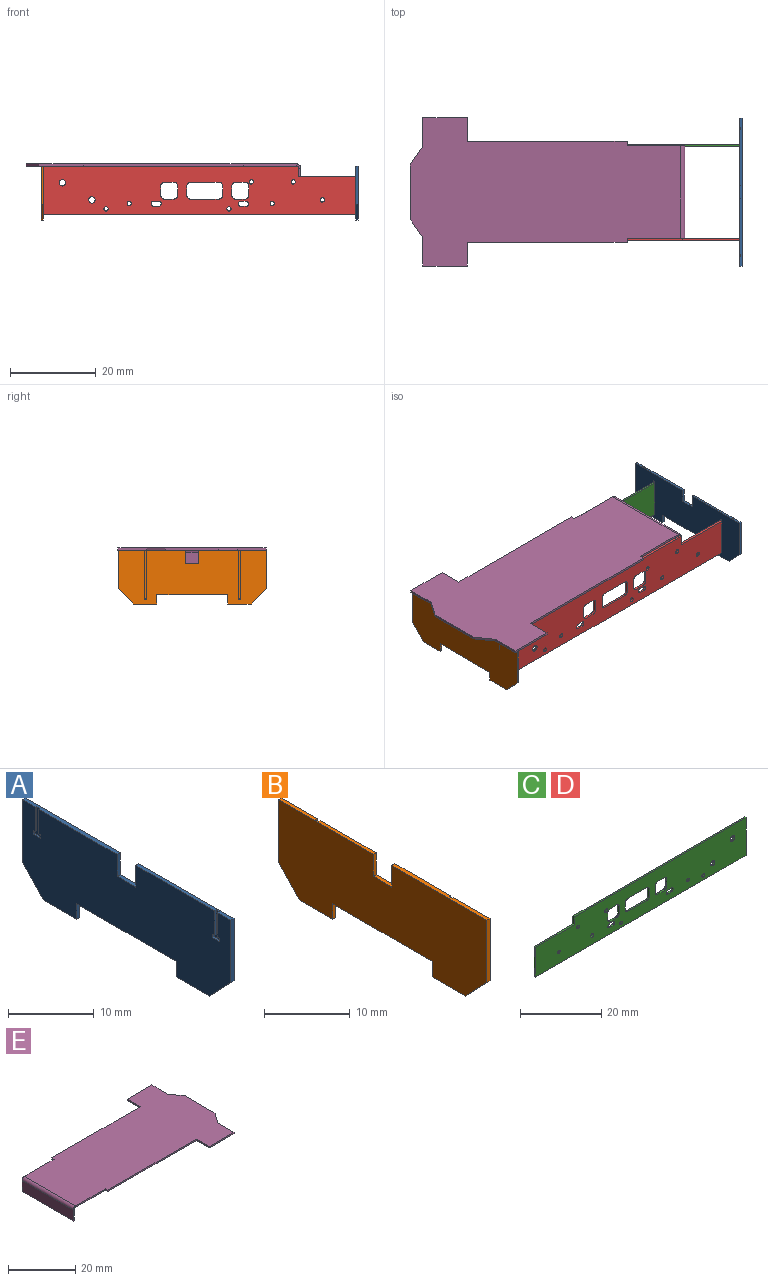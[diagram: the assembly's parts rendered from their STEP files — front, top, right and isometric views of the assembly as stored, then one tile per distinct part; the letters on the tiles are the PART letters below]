
ASSEMBLY  parts=5 mates=12
PART A: 42 faces, bbox 0.5x34.5x12.6 mm
  f0: plane 34.5x12.6mm, normal (-1,0,0), area 371.1mm2, adj f2,f3,f4,f5,f6,f7,f8,f9
  f1: plane 34.5x12.6mm, normal (1,0,0), area 366.4mm2, adj f2,f3,f4,f5,f6,f7,f8,f9
  f2: plane 3.1x0.5mm, normal (0,0,1), area 1.6mm2, adj f0,f1,f3,f23
  f3: plane 3.1x0.5mm, normal (0,1,0), area 1.5mm2, adj f0,f1,f2,f4
  f4: plane 15.7x0.5mm, normal (0,0,1), area 7.7mm2, adj f0,f1,f3,f5,f15,f21,f22
  f5: plane 8.9x0.5mm, normal (0,-1,0), area 4.4mm2, adj f0,f1,f4,f6
  f6: plane 3.7x3.5mm, normal (0,-0.73,-0.69), area 2.5mm2, adj f0,f1,f5,f7
  f7: plane 5.5x0.5mm, normal (0,0,-1), area 2.8mm2, adj f0,f1,f6,f8
  f8: plane 2.2x0.5mm, normal (0,1,0), area 1.1mm2, adj f0,f1,f7,f9
  f9: plane 16.5x0.5mm, normal (0,0,-1), area 8.2mm2, adj f0,f1,f8,f28
  f10: plane 0.5x0.25mm, normal (0,0,-1), area 0.1mm2, adj f1,f11,f13,f14
  f11: plane 9.4x0.25mm, normal (0,1,0), area 2.4mm2, adj f1,f10,f12,f14
  f12: plane 0.5x0.25mm, normal (0,0,1), area 0.1mm2, adj f1,f11,f13,f14
  f13: plane 9.4x0.25mm, normal (0,-1,0), area 2.4mm2, adj f1,f10,f12,f14
  f14: plane 9.4x0.5mm, normal (1,0,0), area 4.7mm2, adj f10,f11,f12,f13
  f15: plane 3.5x0.25mm, normal (0,-1,0), area 0.9mm2, adj f0,f4,f16,f22
  f16: plane 0.35x0.25mm, normal (0,0,-1), area 0.1mm2, adj f0,f15,f17,f22
  f17: plane 0.5x0.25mm, normal (0,-1,0), area 0.1mm2, adj f0,f16,f18,f22
  f18: plane 1.2x0.25mm, normal (0,0,1), area 0.3mm2, adj f0,f17,f19,f22
  f19: plane 0.5x0.25mm, normal (0,1,0), area 0.1mm2, adj f0,f18,f20,f22
  f20: plane 0.35x0.25mm, normal (0,0,-1), area 0.1mm2, adj f0,f19,f21,f22
  f21: plane 3.5x0.25mm, normal (0,1,0), area 0.9mm2, adj f0,f4,f20,f22
  f22: plane 4x1.2mm, normal (-1,0,0), area 2.3mm2, adj f4,f15,f16,f17,f18,f19,f20,f21
  f23: plane 3.1x0.5mm, normal (0,-1,0), area 1.5mm2, adj f0,f1,f2,f24
  f24: plane 15.7x0.5mm, normal (0,0,1), area 7.7mm2, adj f0,f1,f23,f25,f34,f40,f41
  f25: plane 8.9x0.5mm, normal (0,1,0), area 4.4mm2, adj f0,f1,f24,f26
  f26: plane 3.7x3.5mm, normal (0,0.73,-0.69), area 2.5mm2, adj f0,f1,f25,f27
  f27: plane 5.5x0.5mm, normal (0,0,-1), area 2.8mm2, adj f0,f1,f26,f28
  f28: plane 2.2x0.5mm, normal (0,-1,0), area 1.1mm2, adj f0,f1,f9,f27
  f29: plane 0.5x0.25mm, normal (0,0,-1), area 0.1mm2, adj f1,f30,f32,f33
  f30: plane 9.4x0.25mm, normal (0,-1,0), area 2.4mm2, adj f1,f29,f31,f33
  f31: plane 0.5x0.25mm, normal (0,0,1), area 0.1mm2, adj f1,f30,f32,f33
  f32: plane 9.4x0.25mm, normal (0,1,0), area 2.4mm2, adj f1,f29,f31,f33
  f33: plane 9.4x0.5mm, normal (1,0,0), area 4.7mm2, adj f29,f30,f31,f32
  f34: plane 3.5x0.25mm, normal (0,1,0), area 0.9mm2, adj f0,f24,f35,f41
  f35: plane 0.35x0.25mm, normal (0,0,-1), area 0.1mm2, adj f0,f34,f36,f41
  f36: plane 0.5x0.25mm, normal (0,1,0), area 0.1mm2, adj f0,f35,f37,f41
  f37: plane 1.2x0.25mm, normal (0,0,1), area 0.3mm2, adj f0,f36,f38,f41
  f38: plane 0.5x0.25mm, normal (0,-1,0), area 0.1mm2, adj f0,f37,f39,f41
  f39: plane 0.35x0.25mm, normal (0,0,-1), area 0.1mm2, adj f0,f38,f40,f41
  f40: plane 3.5x0.25mm, normal (0,-1,0), area 0.9mm2, adj f0,f24,f39,f41
  f41: plane 4x1.2mm, normal (-1,0,0), area 2.3mm2, adj f24,f34,f35,f36,f37,f38,f39,f40
PART B: 24 faces, bbox 0.5x34.5x12.6 mm
  f0: plane 3.1x0.5mm, normal (0,0,1), area 1.6mm2, adj f1,f8,f9,f14
  f1: plane 3.1x0.5mm, normal (0,1,0), area 1.5mm2, adj f0,f2,f8,f9
  f2: plane 15.7x0.5mm, normal (0,0,1), area 7.7mm2, adj f1,f3,f8,f9,f10,f12,f13
  f3: plane 8.9x0.5mm, normal (0,-1,0), area 4.4mm2, adj f2,f4,f8,f9
  f4: plane 3.7x3.5mm, normal (0,-0.73,-0.69), area 2.5mm2, adj f3,f5,f8,f9
  f5: plane 5.5x0.5mm, normal (0,0,-1), area 2.8mm2, adj f4,f6,f8,f9
  f6: plane 2.2x0.5mm, normal (0,1,0), area 1.1mm2, adj f5,f7,f8,f9
  f7: plane 16.5x0.5mm, normal (0,0,-1), area 8.2mm2, adj f6,f8,f9,f19
  f8: plane 34.5x12.6mm, normal (1,0,0), area 364.2mm2, adj f0,f1,f2,f3,f4,f5,f6,f7
  f9: plane 34.5x12.6mm, normal (-1,0,0), area 375.8mm2, adj f0,f1,f2,f3,f4,f5,f6,f7
  f10: plane 11.6x0.25mm, normal (0,1,0), area 2.9mm2, adj f2,f8,f11,f13
  f11: plane 0.5x0.25mm, normal (0,0,1), area 0.1mm2, adj f8,f10,f12,f13
  f12: plane 11.6x0.25mm, normal (0,-1,0), area 2.9mm2, adj f2,f8,f11,f13
  f13: plane 11.6x0.5mm, normal (1,0,0), area 5.8mm2, adj f2,f10,f11,f12
  f14: plane 3.1x0.5mm, normal (0,-1,0), area 1.5mm2, adj f0,f8,f9,f15
  f15: plane 15.7x0.5mm, normal (0,0,1), area 7.7mm2, adj f8,f9,f14,f16,f20,f22,f23
  f16: plane 8.9x0.5mm, normal (0,1,0), area 4.4mm2, adj f8,f9,f15,f17
  f17: plane 3.7x3.5mm, normal (0,0.73,-0.69), area 2.5mm2, adj f8,f9,f16,f18
  f18: plane 5.5x0.5mm, normal (0,0,-1), area 2.8mm2, adj f8,f9,f17,f19
  f19: plane 2.2x0.5mm, normal (0,-1,0), area 1.1mm2, adj f7,f8,f9,f18
  f20: plane 11.6x0.25mm, normal (0,-1,0), area 2.9mm2, adj f8,f15,f21,f23
  f21: plane 0.5x0.25mm, normal (0,0,1), area 0.1mm2, adj f8,f20,f22,f23
  f22: plane 11.6x0.25mm, normal (0,1,0), area 2.9mm2, adj f8,f15,f21,f23
  f23: plane 11.6x0.5mm, normal (1,0,0), area 5.8mm2, adj f15,f20,f21,f22
PART C: 49 faces, bbox 73.5x0.5x11.4 mm
  f0: plane 73.5x11.4mm, normal (0,-1,0), area 729.9mm2, adj f2,f3,f4,f5,f6,f7,f8,f9
  f1: plane 73.5x11.4mm, normal (0,1,0), area 729.9mm2, adj f2,f3,f4,f5,f6,f7,f8,f9
  f2: plane 9x0.5mm, normal (-1,0,0), area 4.5mm2, adj f0,f1,f3,f7
  f3: plane 73.5x0.5mm, normal (0,0,-1), area 36.8mm2, adj f0,f1,f2,f4
  f4: plane 11.4x0.5mm, normal (1,0,0), area 5.7mm2, adj f0,f1,f3,f5
  f5: plane 59.9x0.5mm, normal (0,0,1), area 29.9mm2, adj f0,f1,f4,f6
  f6: plane 2.4x0.5mm, normal (-1,0,0), area 1.2mm2, adj f0,f1,f5,f7
  f7: plane 13.6x0.5mm, normal (0,0,1), area 6.8mm2, adj f0,f1,f2,f6
  f8: plane 2.3x0.5mm, normal (0,0,-1), area 1.2mm2, adj f0,f1,f28,f31
  f9: plane 2.3x0.5mm, normal (1,0,0), area 1.2mm2, adj f0,f1,f28,f29
  f10: plane 2.3x0.5mm, normal (0,0,1), area 1.1mm2, adj f0,f1,f29,f30
  f11: plane 2.3x0.5mm, normal (-1,0,0), area 1.1mm2, adj f0,f1,f30,f31
  f12: plane 6.7x0.5mm, normal (0,0,-1), area 3.4mm2, adj f0,f1,f24,f27
  f13: plane 2.3x0.5mm, normal (1,0,0), area 1.2mm2, adj f0,f1,f24,f25
  f14: plane 6.7x0.5mm, normal (0,0,1), area 3.3mm2, adj f0,f1,f25,f26
  f15: plane 2.3x0.5mm, normal (-1,0,0), area 1.1mm2, adj f0,f1,f26,f27
  f16: plane 2.3x0.5mm, normal (0,0,-1), area 1.1mm2, adj f0,f1,f20,f23
  f17: plane 2.3x0.5mm, normal (1,0,0), area 1.2mm2, adj f0,f1,f20,f21
  f18: plane 2.3x0.5mm, normal (0,0,1), area 1.1mm2, adj f0,f1,f21,f22
  f19: plane 2.3x0.5mm, normal (-1,0,0), area 1.1mm2, adj f0,f1,f22,f23
  f20: cylinder r=0.8mm len=0.8mm, axis (0,-1,0), area 0.6mm2, adj f0,f1,f16,f17
  f21: cylinder r=0.8mm len=0.8mm, axis (0,1,0), area 0.6mm2, adj f0,f1,f17,f18
  f22: cylinder r=0.8mm len=0.8mm, axis (0,-1,0), area 0.6mm2, adj f0,f1,f18,f19
  f23: cylinder r=0.8mm len=0.8mm, axis (0,1,0), area 0.6mm2, adj f0,f1,f16,f19
  f24: cylinder r=0.8mm len=0.8mm, axis (0,-1,0), area 0.6mm2, adj f0,f1,f12,f13
  f25: cylinder r=0.8mm len=0.8mm, axis (0,1,0), area 0.6mm2, adj f0,f1,f13,f14
  f26: cylinder r=0.8mm len=0.8mm, axis (0,-1,0), area 0.6mm2, adj f0,f1,f14,f15
  f27: cylinder r=0.8mm len=0.8mm, axis (0,1,0), area 0.6mm2, adj f0,f1,f12,f15
  f28: cylinder r=0.8mm len=0.8mm, axis (0,-1,0), area 0.6mm2, adj f0,f1,f8,f9
  f29: cylinder r=0.8mm len=0.8mm, axis (0,1,0), area 0.6mm2, adj f0,f1,f9,f10
  f30: cylinder r=0.8mm len=0.8mm, axis (0,-1,0), area 0.6mm2, adj f0,f1,f10,f11
  f31: cylinder r=0.8mm len=0.8mm, axis (0,1,0), area 0.6mm2, adj f0,f1,f8,f11
  f32: cylinder r=0.5mm len=1mm, axis (0,-1,0), area 1.6mm2, adj f0,f1
  f33: cylinder r=0.5mm len=1mm, axis (0,-1,0), area 1.6mm2, adj f0,f1
  f34: cylinder r=0.5mm len=1mm, axis (0,-1,0), area 1.6mm2, adj f0,f1
  f35: cylinder r=0.5mm len=1mm, axis (0,-1,0), area 1.6mm2, adj f0,f1
  f36: cylinder r=0.5mm len=1mm, axis (0,-1,0), area 1.6mm2, adj f0,f1
  f37: cylinder r=0.5mm len=1mm, axis (0,-1,0), area 1.6mm2, adj f0,f1
  f38: cylinder r=0.5mm len=1mm, axis (0,-1,0), area 1.6mm2, adj f0,f1
  f39: cylinder r=0.75mm len=1.5mm, axis (0,-1,0), area 2.4mm2, adj f0,f1
  f40: cylinder r=0.75mm len=1.5mm, axis (0,-1,0), area 2.4mm2, adj f0,f1
  f41: plane 1.2x0.5mm, normal (0,0,-1), area 0.6mm2, adj f0,f1,f42,f44
  f42: cylinder r=0.6mm len=1.2mm, axis (0,-1,0), area 0.9mm2, adj f0,f1,f41,f43
  f43: plane 1.2x0.5mm, normal (0,0,1), area 0.6mm2, adj f0,f1,f42,f44
  f44: cylinder r=0.6mm len=1.2mm, axis (0,-1,0), area 0.9mm2, adj f0,f1,f41,f43
  f45: plane 1.2x0.5mm, normal (0,0,-1), area 0.6mm2, adj f0,f1,f46,f48
  f46: cylinder r=0.6mm len=1.2mm, axis (0,-1,0), area 0.9mm2, adj f0,f1,f45,f47
  f47: plane 1.2x0.5mm, normal (0,0,1), area 0.6mm2, adj f0,f1,f46,f48
  f48: cylinder r=0.6mm len=1.2mm, axis (0,-1,0), area 0.9mm2, adj f0,f1,f45,f47
PART D: same geometry as C
PART E: 26 faces, bbox 64.2x34.6x5 mm
  f0: plane 1x0.5mm, normal (-1,0,0), area 0.5mm2, adj f1,f14,f15,f16
  f1: plane 37.3x0.5mm, normal (0,1,0), area 18.6mm2, adj f0,f2,f15,f16
  f2: plane 5.5x0.5mm, normal (-1,0,0), area 2.8mm2, adj f1,f3,f15,f16
  f3: plane 10.4x0.5mm, normal (0,1,0), area 5.2mm2, adj f2,f4,f15,f16
  f4: plane 6.7x0.5mm, normal (1,0,0), area 3.3mm2, adj f3,f5,f15,f16
  f5: plane 4.3x3mm, normal (0.82,0.57,0), area 2.6mm2, adj f4,f6,f15,f16
  f6: plane 12.6x0.5mm, normal (1,0,0), area 6.3mm2, adj f5,f7,f15,f16
  f7: plane 4.3x3mm, normal (0.82,-0.57,0), area 2.6mm2, adj f6,f8,f15,f16
  f8: plane 6.7x0.5mm, normal (1,0,0), area 3.3mm2, adj f7,f9,f15,f16
  f9: plane 10.4x0.5mm, normal (0,-1,0), area 5.2mm2, adj f8,f10,f15,f16
  f10: plane 5.5x0.5mm, normal (-1,0,0), area 2.8mm2, adj f9,f11,f15,f16
  f11: plane 37.3x0.5mm, normal (0,-1,0), area 18.6mm2, adj f10,f12,f15,f16
  f12: plane 1x0.5mm, normal (-1,0,0), area 0.5mm2, adj f11,f13,f15,f16
  f13: plane 12.5x0.5mm, normal (0,-1,0), area 6.2mm2, adj f12,f15,f16,f23
  f14: plane 12.5x0.5mm, normal (0,1,0), area 6.2mm2, adj f0,f15,f16,f22
  f15: plane 63.2x34.6mm, normal (0,0,-1), area 1560.8mm2, adj f0,f1,f2,f3,f4,f5,f6,f7
  f16: plane 63.2x34.6mm, normal (0,0,1), area 1560.8mm2, adj f0,f1,f2,f3,f4,f5,f6,f7
  f17: plane 21.6x0.5mm, normal (0,0,-1), area 10.8mm2, adj f18,f19,f20,f21
  f18: plane 4x0.5mm, normal (0,1,0), area 2mm2, adj f17,f20,f21,f22
  f19: plane 4x0.5mm, normal (0,-1,0), area 2mm2, adj f17,f20,f21,f23
  f20: plane 21.6x4mm, normal (1,0,0), area 86.4mm2, adj f17,f18,f19,f25
  f21: plane 21.6x4mm, normal (-1,0,0), area 86.4mm2, adj f17,f18,f19,f24
  f22: plane 1x1mm, normal (0,1,0), area 0.6mm2, adj f14,f18,f24,f25
  f23: plane 1x1mm, normal (0,-1,0), area 0.6mm2, adj f13,f19,f24,f25
  f24: cylinder r=1mm len=21.6mm, axis (0,1,0), area 33.9mm2, adj f16,f21,f22,f23
  f25: cylinder r=0.5mm len=21.6mm, axis (0,1,0), area 17mm2, adj f15,f20,f22,f23
PLACE A rot(axis=(0,0,1),180deg) t=(73.5,-0.05,0)mm
PLACE B t=(-0.5,-0.05,0)mm
PLACE C rot(axis=(0,0,1),180deg) t=(73.25,10.7,-11.4)mm
PLACE D rot(axis=(0,0,1),180deg) t=(73.25,-11.3,-11.4)mm
PLACE E rot(axis=(0,0,-1),180deg) t=(60.15,0,0)mm
MATE planar B.f15 <-> C.f5  axis (0,0,1) through (-0.25,9.32,0)mm
MATE planar B.f2 <-> D.f5  axis (0,0,1) through (-0.25,-9.42,0)mm
MATE planar B.f15 <-> A.f4  axis (0,0,1) through (-0.25,9.32,0)mm
MATE planar B.f13 <-> D.f4  axis (1,0,0) through (-0.25,-11.05,-5.8)mm
MATE planar B.f3 <-> A.f25  axis (0,-1,0) through (-0.25,-17.3,-4.45)mm
MATE planar B.f22 <-> C.f36  axis (0,1,0) through (-0.13,10.7,-5.8)mm
MATE planar D.f5 <-> E.f15  axis (0,0,1) through (29.7,-11.05,0)mm
MATE planar B.f10 <-> D.f1  axis (0,1,0) through (-0.13,-11.3,-5.8)mm
MATE planar C.f2 <-> A.f14  axis (1,0,0) through (73.25,10.95,-6.9)mm
MATE planar E.f20 <-> D.f6  axis (-1,0,0) through (59.65,0,-2.5)mm
MATE planar B.f23 <-> C.f4  axis (1,0,0) through (-0.25,10.95,-5.8)mm
MATE planar E.f3 <-> B.f3  axis (0,-1,0) through (4.15,-17.3,0.25)mm
